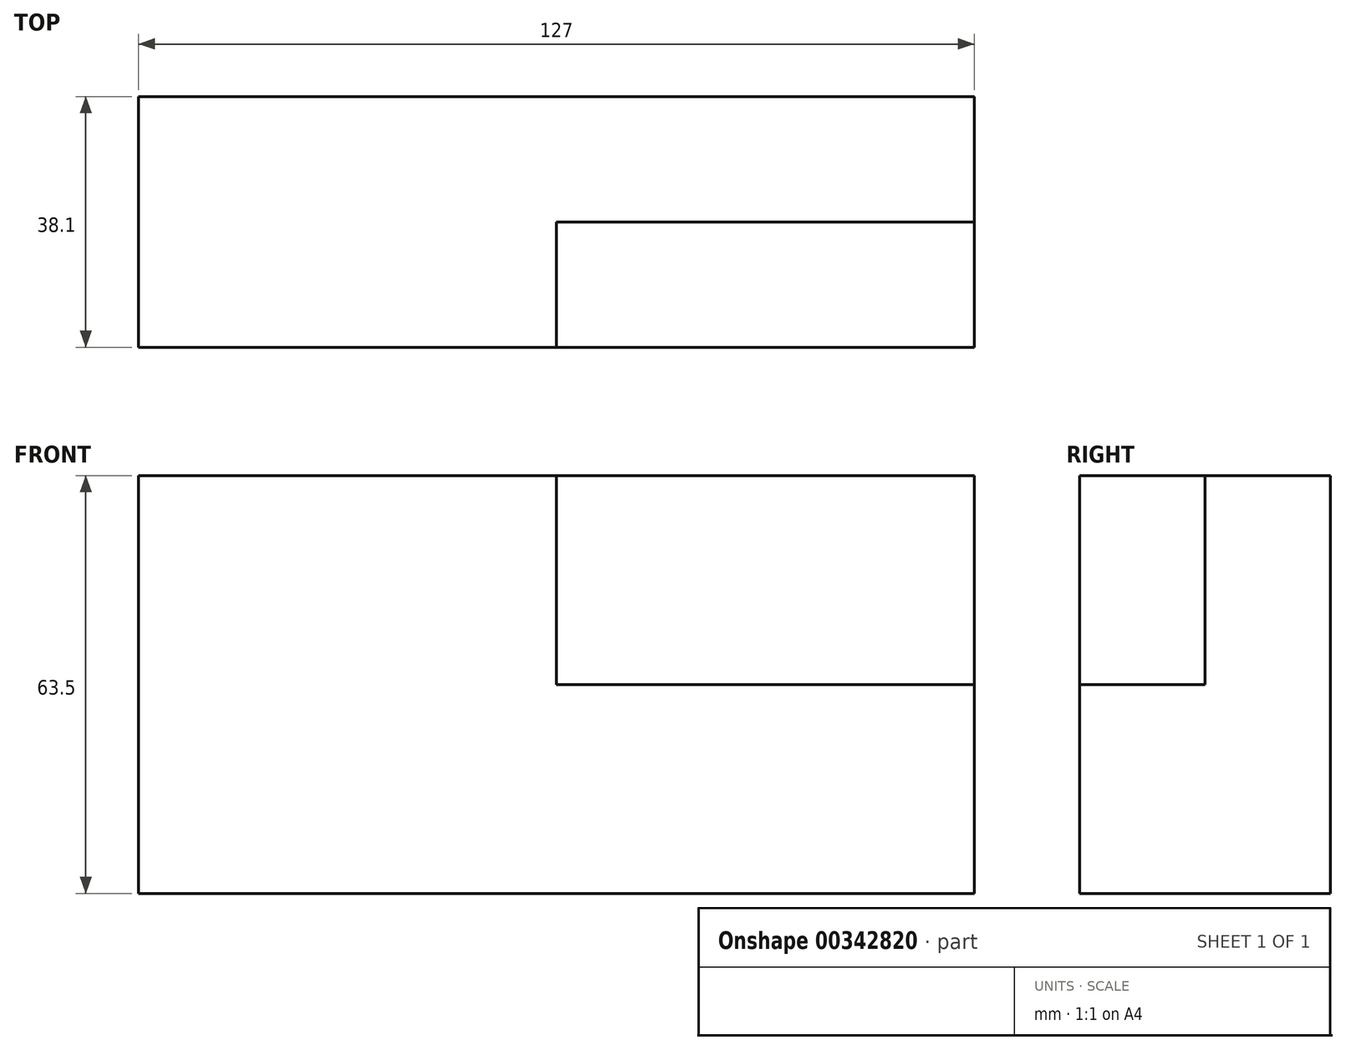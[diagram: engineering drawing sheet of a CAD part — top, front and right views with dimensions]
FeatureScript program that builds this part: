
annotation { "Feature Type Name" : "Feature", "Feature Type Description" : "" }
export const myFeature = defineFeature(function(context is Context, id is Id, definition is map)
    precondition{}
    {
        {
            var Q0;
            Q0=qCreatedBy(makeId("Top.planeOp"),FACE);
            var sketch = newSketch(context, id + "F0", { "sketchPlane" : qUnion([Q0])});
            skLineSegment(sketch, "E0", {"start": v(-51.64, -17.28) * mm, "end": v(11.86, -17.28) * mm});
            skLineSegment(sketch, "E1", {"start": v(-51.64, -17.28) * mm, "end": v(-51.64, 20.82) * mm});
            skLineSegment(sketch, "E2", {"start": v(-51.64, 20.82) * mm, "end": v(75.36, 20.82) * mm});
            skLineSegment(sketch, "E3", {"start": v(75.36, 20.82) * mm, "end": v(75.36, 1.77) * mm});
            skLineSegment(sketch, "E4", {"start": v(75.36, 1.77) * mm, "end": v(11.86, 1.77) * mm});
            skLineSegment(sketch, "E5", {"start": v(11.86, 1.77) * mm, "end": v(11.86, -17.28) * mm});
            skSolve(sketch);
        }
        {
            var Q0;
            Q0=makeQuery(id+"F0.imprint","IMPRINT",FACE,{"disambiguationData":[TD([[makeQuery(id+"F0.imprint","IMPRINT",EDGE,{"derivedFrom":sQuery(id+"F0.wireOp",EDGE,"E0")}),1.0]])]});
            extrude(context, id + "F1", {"entities" : qUnion([Q0]), "depth" : 31.75 * mm});
        }
        {
            var Q0;
            Q0=makeQuery(id+"F1.opExtrude","CAP_FACE",FACE,{"disambiguationData":[OSD([sQuery(id+"F0.wireOp",EDGE,"E0"),sQuery(id+"F0.wireOp",EDGE,"E1"),sQuery(id+"F0.wireOp",EDGE,"E2"),sQuery(id+"F0.wireOp",EDGE,"E3"),sQuery(id+"F0.wireOp",EDGE,"E4"),sQuery(id+"F0.wireOp",EDGE,"E5")])],"isStart":true});
            var sketch = newSketch(context, id + "F2", { "sketchPlane" : qUnion([Q0])});
            skLineSegment(sketch, "E6", {"start": v(-51.64, 17.28) * mm, "end": v(-51.64, -20.82) * mm});
            skLineSegment(sketch, "E7", {"start": v(-51.64, -20.82) * mm, "end": v(75.36, -20.82) * mm});
            skLineSegment(sketch, "E8", {"start": v(75.36, -20.82) * mm, "end": v(75.36, 17.28) * mm});
            skLineSegment(sketch, "E9", {"start": v(75.36, 17.28) * mm, "end": v(-51.64, 17.28) * mm});
            skSolve(sketch);
        }
        {
            var Q0;
            {var subQ1=makeQuery(id+"F1.opExtrude","CAP_EDGE",EDGE,{"disambiguationData":[OSD([sQuery(id+"F0.wireOp",EDGE,"E4")])],"isStart":true});Q0=makeQuery(id+"F2.imprint","IMPRINT",FACE,{"disambiguationData":[TD([[makeQuery(id+"F2.imprint","IMPRINT",EDGE,{"derivedFrom":subQ1}),-1.0]])]});}
            var Q1;
            {var subQ4=sQuery(id+"F2.wireOp",EDGE,"E6");Q1=makeQuery(id+"F2.imprint","IMPRINT",FACE,{"disambiguationData":[TD([[makeQuery(id+"F2.imprint","IMPRINT",EDGE,{"derivedFrom":subQ4}),1.0]])]});}
            extrude(context, id + "F3", {"entities" : qUnion([Q0, Q1]), "operationType" : NewBodyOperationType.ADD, "depth" : 31.75 * mm});
        }
    });
